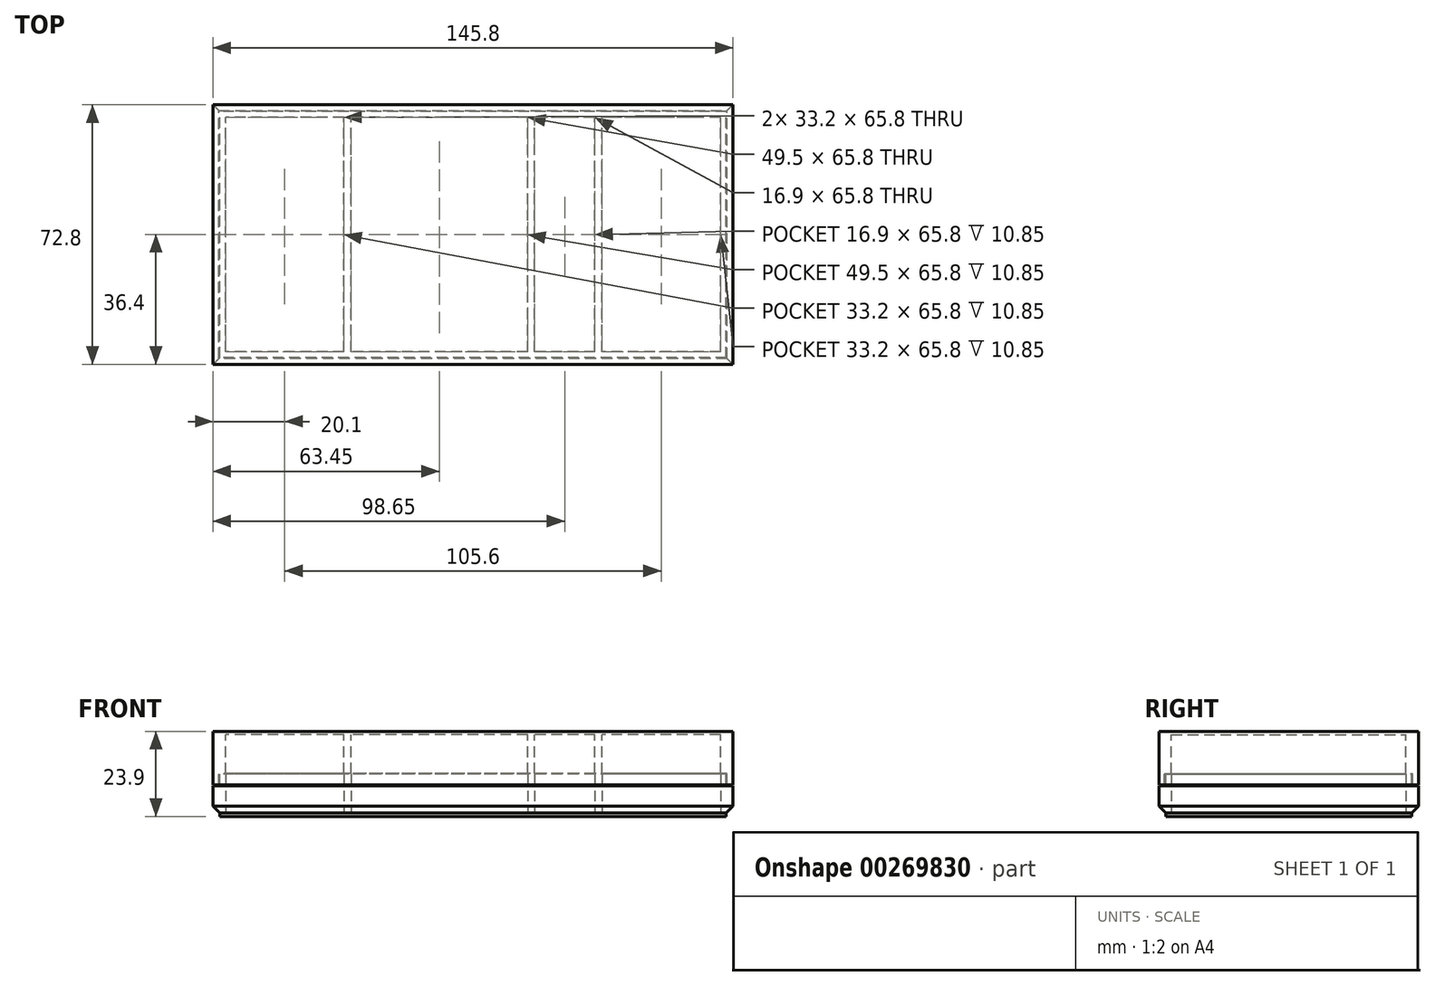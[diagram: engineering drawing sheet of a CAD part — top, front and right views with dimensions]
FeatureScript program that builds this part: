
annotation { "Feature Type Name" : "Feature", "Feature Type Description" : "" }
export const myFeature = defineFeature(function(context is Context, id is Id, definition is map)
    precondition{}
    {
        {
            assignVariable(context, id + "F0", {"name" : "chaff", "anyValue" : .3});
        }
        {
            assignVariable(context, id + "F1", {"name" : "basethick", "anyValue" : 1});
        }
        {
            assignVariable(context, id + "F2", {"name" : "unitTokenHeight", "anyValue" : 20.5});
        }
        {
            assignVariable(context, id + "F3", {"name" : "lidrimdepth", "anyValue" : 3});
        }
        {
            var Q0;
            Q0=qCreatedBy(makeId("Top.planeOp"),FACE);
            var sketch = newSketch(context, id + "F4", { "sketchPlane" : qUnion([Q0])});
            skLineSegment(sketch, "E0.bottom", {"start": v(72.9, -36.4) * mm, "end": v(-72.9, -36.4) * mm});
            skLineSegment(sketch, "E0.top", {"start": v(72.9, 36.4) * mm, "end": v(-72.9, 36.4) * mm});
            skLineSegment(sketch, "E0.left", {"start": v(72.9, -36.4) * mm, "end": v(72.9, 36.4) * mm});
            skLineSegment(sketch, "E0.right", {"start": v(-72.9, -36.4) * mm, "end": v(-72.9, 36.4) * mm});
            skPoint(sketch, "E0.middle", {"position": v(0, 0) * mm});
            skSolve(sketch);
        }
        {
            var Q0;
            Q0=qSketchRegion(id+"F4",true);
            extrude(context, id + "F5", {"entities" : qUnion([Q0]), "depth" : (getVariable(context, 'basethick')) * mm});
        }
        {
            var Q0;
            Q0=makeQuery(id+"F5.opExtrude","CAP_FACE",FACE,{"disambiguationData":[OSD([sQuery(id+"F4.wireOp",EDGE,"E0.bottom"),sQuery(id+"F4.wireOp",EDGE,"E0.top"),sQuery(id+"F4.wireOp",EDGE,"E0.left"),sQuery(id+"F4.wireOp",EDGE,"E0.right")])],"isStart":false});
            var sketch = newSketch(context, id + "F6", { "sketchPlane" : qUnion([Q0])});
            skLineSegment(sketch, "E1.bottom", {"start": v(69.4, -32.9) * mm, "end": v(-69.4, -32.9) * mm});
            skLineSegment(sketch, "E1.top", {"start": v(69.4, 32.9) * mm, "end": v(-69.4, 32.9) * mm});
            skLineSegment(sketch, "E1.left", {"start": v(69.4, -32.9) * mm, "end": v(69.4, 32.9) * mm});
            skLineSegment(sketch, "E1.right", {"start": v(-69.4, -32.9) * mm, "end": v(-69.4, 32.9) * mm});
            skPoint(sketch, "E1.middle", {"position": v(0, 0) * mm});
            skLineSegment(sketch, "E2", {"start": v(0, 32.9) * mm, "end": v(0, 36.4) * mm, "construction": true});
            skLineSegment(sketch, "E3.0", {"start": v(-72.9, -36.4) * mm, "end": v(-72.9, 36.4) * mm});
            skLineSegment(sketch, "E4.0", {"start": v(72.9, -36.4) * mm, "end": v(-72.9, -36.4) * mm});
            skLineSegment(sketch, "E5.0", {"start": v(72.9, -36.4) * mm, "end": v(72.9, 36.4) * mm});
            skLineSegment(sketch, "E6.0", {"start": v(72.9, 36.4) * mm, "end": v(-72.9, 36.4) * mm});
            skLineSegment(sketch, "E7", {"start": v(-72.9, 0) * mm, "end": v(-69.4, 0) * mm, "construction": true});
            skSolve(sketch);
        }
        {
            var Q0;
            Q0=qSketchRegion(id+"F6",true);
            extrude(context, id + "F7", {"entities" : qUnion([Q0]), "operationType" : NewBodyOperationType.ADD, "depth" : (getVariable(context, 'unitTokenHeight') / 2 + getVariable(context, 'chaff') * 2) * mm});
        }
        {
            var Q0;
            Q0=makeQuery(id+"F7.opExtrude","SWEPT_FACE",FACE,{"disambiguationData":[OSD([sQuery(id+"F6.wireOp",EDGE,"E1.top")])]});
            var sketch = newSketch(context, id + "F8", { "sketchPlane" : qUnion([Q0])});
            skLineSegment(sketch, "E8", {"start": v(-69.4, 11.85) * mm, "end": v(-36.2, 11.85) * mm, "construction": true});
            skLineSegment(sketch, "E9.bottom", {"start": v(-36.2, 11.85) * mm, "end": v(-34.2, 11.85) * mm});
            skLineSegment(sketch, "E9.top", {"start": v(-36.2, 1) * mm, "end": v(-34.2, 1) * mm});
            skLineSegment(sketch, "E9.left", {"start": v(-36.2, 11.85) * mm, "end": v(-36.2, 1) * mm});
            skLineSegment(sketch, "E9.right", {"start": v(-34.2, 11.85) * mm, "end": v(-34.2, 1) * mm});
            skLineSegment(sketch, "E10", {"start": v(-34.2, 11.85) * mm, "end": v(15.3, 11.85) * mm, "construction": true});
            skLineSegment(sketch, "E11.bottom", {"start": v(15.3, 11.85) * mm, "end": v(17.3, 11.85) * mm});
            skLineSegment(sketch, "E11.top", {"start": v(15.3, 1) * mm, "end": v(17.3, 1) * mm});
            skLineSegment(sketch, "E11.left", {"start": v(15.3, 11.85) * mm, "end": v(15.3, 1) * mm});
            skLineSegment(sketch, "E11.right", {"start": v(17.3, 11.85) * mm, "end": v(17.3, 1) * mm});
            skLineSegment(sketch, "E12", {"start": v(17.3, 11.85) * mm, "end": v(34.2, 11.85) * mm, "construction": true});
            skLineSegment(sketch, "E13.bottom", {"start": v(34.2, 11.85) * mm, "end": v(36.2, 11.85) * mm});
            skLineSegment(sketch, "E13.top", {"start": v(34.2, 1) * mm, "end": v(36.2, 1) * mm});
            skLineSegment(sketch, "E13.left", {"start": v(34.2, 11.85) * mm, "end": v(34.2, 1) * mm});
            skLineSegment(sketch, "E13.right", {"start": v(36.2, 11.85) * mm, "end": v(36.2, 1) * mm});
            skLineSegment(sketch, "E14", {"start": v(36.2, 11.85) * mm, "end": v(69.4, 11.85) * mm, "construction": true});
            skSolve(sketch);
        }
        {
            var Q0;
            Q0=makeQuery(id+"F8.imprint","IMPRINT",FACE,{"disambiguationData":[TD([[makeQuery(id+"F8.imprint","IMPRINT",EDGE,{"derivedFrom":sQuery(id+"F8.wireOp",EDGE,"E9.bottom")}),1.0]])]});
            var Q1;
            Q1=makeQuery(id+"F8.imprint","IMPRINT",FACE,{"disambiguationData":[TD([[makeQuery(id+"F8.imprint","IMPRINT",EDGE,{"derivedFrom":sQuery(id+"F8.wireOp",EDGE,"E11.bottom")}),1.0]])]});
            var Q2;
            Q2=makeQuery(id+"F8.imprint","IMPRINT",FACE,{"disambiguationData":[TD([[makeQuery(id+"F8.imprint","IMPRINT",EDGE,{"derivedFrom":sQuery(id+"F8.wireOp",EDGE,"E13.bottom")}),1.0]])]});
            var Q3;
            Q3=makeQuery(id+"F7.opExtrude","SWEPT_FACE",FACE,{"disambiguationData":[OSD([sQuery(id+"F6.wireOp",EDGE,"E1.bottom")])]});
            extrude(context, id + "F9", {"entities" : qUnion([Q0, Q1, Q2]), "operationType" : NewBodyOperationType.ADD, "endBound" : BoundingType.UP_TO_SURFACE, "endBoundEntityFace" : qUnion([Q3]), "depth" : 25 * mm});
        }
        {
            var Q0;
            {var subQ0=sQuery(id+"F8.wireOp",EDGE,"b7063ba6-163c-4e90-9692-3a0a1676d49b.0");var subQ1=sQuery(id+"F8.wireOp",EDGE,"5b0bd29a-2a72-4641-92b4-ce3cebaaf724.1.0.1");var subQ2=sQuery(id+"F8.wireOp",EDGE,"5b0bd29a-2a72-4641-92b4-ce3cebaaf724.2.0.1");Q0=makeQuery(id+"F9.boolean.opBoolean","MERGE",FACE,{"derivedFrom":[makeQuery(id+"F7.opExtrude","CAP_FACE",FACE,{"disambiguationData":[OSD([sQuery(id+"F6.wireOp",EDGE,"E1.bottom"),sQuery(id+"F6.wireOp",EDGE,"E1.top"),sQuery(id+"F6.wireOp",EDGE,"E1.left"),sQuery(id+"F6.wireOp",EDGE,"E1.right"),sQuery(id+"F6.wireOp",EDGE,"E3.0"),sQuery(id+"F6.wireOp",EDGE,"E4.0"),sQuery(id+"F6.wireOp",EDGE,"E5.0"),sQuery(id+"F6.wireOp",EDGE,"E6.0")])],"isStart":false}),makeQuery(id+"F9.opExtrude","SWEPT_FACE",FACE,{"disambiguationData":[OSD([subQ0]),TDD([makeQuery(id+"F8.imprint","IMPRINT",EDGE,{"disambiguationData":[TD([[makeQuery(id+"F8.imprint","INTERSECT",VERTEX,{"derivedFrom":[sQuery(id+"F8.wireOp",EDGE,"ed8556cc-012e-414f-a647-4d99696943b9.0"),subQ0]}),-1.0]])],"derivedFrom":subQ0})])]}),makeQuery(id+"F9.opExtrude","SWEPT_FACE",FACE,{"disambiguationData":[OSD([subQ0]),TDD([makeQuery(id+"F8.imprint","IMPRINT",EDGE,{"disambiguationData":[TD([[makeQuery(id+"F8.imprint","INTERSECT",VERTEX,{"disambiguationData":[OD(1.0)],"derivedFrom":[subQ2,subQ0]}),1.0]])],"derivedFrom":subQ0})])]}),makeQuery(id+"F9.opExtrude","SWEPT_FACE",FACE,{"disambiguationData":[OSD([subQ0]),TDD([makeQuery(id+"F8.imprint","IMPRINT",EDGE,{"disambiguationData":[TD([[makeQuery(id+"F8.imprint","INTERSECT",VERTEX,{"disambiguationData":[OD(1.0)],"derivedFrom":[subQ1,subQ0]}),1.0]])],"derivedFrom":subQ0})])]}),makeQuery(id+"F9.opExtrude","SWEPT_FACE",FACE,{"disambiguationData":[OSD([subQ0]),TDD([makeQuery(id+"F8.imprint","IMPRINT",EDGE,{"disambiguationData":[TD([[makeQuery(id+"F8.imprint","INTERSECT",VERTEX,{"derivedFrom":[sQuery(id+"F8.wireOp",EDGE,"CCxmkI6E-hdHg-CZTa-q9Gf-agiM700yoBqG"),subQ0]}),1.0]])],"derivedFrom":subQ0})])]})]});}
            cPlane(context, id + "F10", {"entities" : qUnion([Q0]), "cplaneType" : CPlaneType.OFFSET, "offset" : .1 * mm, "width" : 150 * mm, "height" : 150 * mm});
        }
        {
            var Q0;
            Q0=makeQuery(id+"F5.opExtrude","SWEPT_BODY",BODY,{"disambiguationData":[OSD([sQuery(id+"F4.wireOp",EDGE,"E0.bottom"),sQuery(id+"F4.wireOp",EDGE,"E0.top"),sQuery(id+"F4.wireOp",EDGE,"E0.left"),sQuery(id+"F4.wireOp",EDGE,"E0.right")])]});
            var Q1;
            Q1=qCreatedBy(id+"F10.planeOp",FACE);
            mirror(context, id + "F11", {"entities" : qUnion([Q0]), "mirrorPlane" : qUnion([Q1])});
        }
        {
            var Q0;
            {var subQ0=sQuery(id+"F8.wireOp",EDGE,"b7063ba6-163c-4e90-9692-3a0a1676d49b.0");var subQ1=sQuery(id+"F8.wireOp",EDGE,"5b0bd29a-2a72-4641-92b4-ce3cebaaf724.1.0.1");var subQ2=sQuery(id+"F8.wireOp",EDGE,"5b0bd29a-2a72-4641-92b4-ce3cebaaf724.2.0.1");Q0=makeQuery(id+"F9.boolean.opBoolean","MERGE",FACE,{"derivedFrom":[makeQuery(id+"F7.opExtrude","CAP_FACE",FACE,{"disambiguationData":[OSD([sQuery(id+"F6.wireOp",EDGE,"E1.bottom"),sQuery(id+"F6.wireOp",EDGE,"E1.top"),sQuery(id+"F6.wireOp",EDGE,"E1.left"),sQuery(id+"F6.wireOp",EDGE,"E1.right"),sQuery(id+"F6.wireOp",EDGE,"E3.0"),sQuery(id+"F6.wireOp",EDGE,"E4.0"),sQuery(id+"F6.wireOp",EDGE,"E5.0"),sQuery(id+"F6.wireOp",EDGE,"E6.0")])],"isStart":false}),makeQuery(id+"F9.opExtrude","SWEPT_FACE",FACE,{"disambiguationData":[OSD([subQ0]),TDD([makeQuery(id+"F8.imprint","IMPRINT",EDGE,{"disambiguationData":[TD([[makeQuery(id+"F8.imprint","INTERSECT",VERTEX,{"derivedFrom":[sQuery(id+"F8.wireOp",EDGE,"ed8556cc-012e-414f-a647-4d99696943b9.0"),subQ0]}),-1.0]])],"derivedFrom":subQ0})])]}),makeQuery(id+"F9.opExtrude","SWEPT_FACE",FACE,{"disambiguationData":[OSD([subQ0]),TDD([makeQuery(id+"F8.imprint","IMPRINT",EDGE,{"disambiguationData":[TD([[makeQuery(id+"F8.imprint","INTERSECT",VERTEX,{"disambiguationData":[OD(1.0)],"derivedFrom":[subQ2,subQ0]}),1.0]])],"derivedFrom":subQ0})])]}),makeQuery(id+"F9.opExtrude","SWEPT_FACE",FACE,{"disambiguationData":[OSD([subQ0]),TDD([makeQuery(id+"F8.imprint","IMPRINT",EDGE,{"disambiguationData":[TD([[makeQuery(id+"F8.imprint","INTERSECT",VERTEX,{"disambiguationData":[OD(1.0)],"derivedFrom":[subQ1,subQ0]}),1.0]])],"derivedFrom":subQ0})])]}),makeQuery(id+"F9.opExtrude","SWEPT_FACE",FACE,{"disambiguationData":[OSD([subQ0]),TDD([makeQuery(id+"F8.imprint","IMPRINT",EDGE,{"disambiguationData":[TD([[makeQuery(id+"F8.imprint","INTERSECT",VERTEX,{"derivedFrom":[sQuery(id+"F8.wireOp",EDGE,"CCxmkI6E-hdHg-CZTa-q9Gf-agiM700yoBqG"),subQ0]}),1.0]])],"derivedFrom":subQ0})])]})]});}
            var sketch = newSketch(context, id + "F12", { "sketchPlane" : qUnion([Q0])});
            skLineSegment(sketch, "E15.0", {"start": v(72.9, 36.4) * mm, "end": v(-72.9, 36.4) * mm});
            skLineSegment(sketch, "E16.0", {"start": v(-72.9, -36.4) * mm, "end": v(-72.9, 36.4) * mm});
            skLineSegment(sketch, "E17.0", {"start": v(72.9, -36.4) * mm, "end": v(-72.9, -36.4) * mm});
            skLineSegment(sketch, "E18.0", {"start": v(72.9, -36.4) * mm, "end": v(72.9, 36.4) * mm});
            skLineSegment(sketch, "E19.0", {"start": v(71, 34.5) * mm, "end": v(-71, 34.5) * mm});
            skLineSegment(sketch, "E19.1", {"start": v(71, -34.5) * mm, "end": v(71, 34.5) * mm});
            skLineSegment(sketch, "E19.2", {"start": v(71, -34.5) * mm, "end": v(-71, -34.5) * mm});
            skLineSegment(sketch, "E19.3", {"start": v(-71, -34.5) * mm, "end": v(-71, 34.5) * mm});
            skSolve(sketch);
        }
        {
            var Q0;
            Q0=makeQuery(id+"F12.imprint","IMPRINT",FACE,{"disambiguationData":[TD([[makeQuery(id+"F12.imprint","IMPRINT",EDGE,{"derivedFrom":sQuery(id+"F12.wireOp",EDGE,"E15.0")}),1.0]])]});
            extrude(context, id + "F13", {"entities" : qUnion([Q0]), "operationType" : NewBodyOperationType.REMOVE, "oppositeDirection" : true, "depth" : (getVariable(context, 'lidrimdepth') + getVariable(context, 'chaff')) * mm});
        }
        {
            var Q0;
            Q0=makeQuery(id+"F5.opExtrude","CAP_FACE",FACE,{"disambiguationData":[OSD([sQuery(id+"F4.wireOp",EDGE,"E0.bottom"),sQuery(id+"F4.wireOp",EDGE,"E0.top"),sQuery(id+"F4.wireOp",EDGE,"E0.left"),sQuery(id+"F4.wireOp",EDGE,"E0.right")])],"isStart":true});
            var sketch = newSketch(context, id + "F14", { "sketchPlane" : qUnion([Q0])});
            skLineSegment(sketch, "E20.0", {"start": v(72.9, 36.4) * mm, "end": v(-72.9, 36.4) * mm});
            skLineSegment(sketch, "E21.0", {"start": v(-72.9, 36.4) * mm, "end": v(-72.9, -36.4) * mm});
            skLineSegment(sketch, "E22.0", {"start": v(72.9, 36.4) * mm, "end": v(72.9, -36.4) * mm});
            skLineSegment(sketch, "E23.0", {"start": v(72.9, -36.4) * mm, "end": v(-72.9, -36.4) * mm});
            skLineSegment(sketch, "E24.0", {"start": v(71, 34.5) * mm, "end": v(-71, 34.5) * mm});
            skLineSegment(sketch, "E24.1", {"start": v(71, 34.5) * mm, "end": v(71, -34.5) * mm});
            skLineSegment(sketch, "E24.2", {"start": v(71, -34.5) * mm, "end": v(-71, -34.5) * mm});
            skLineSegment(sketch, "E24.3", {"start": v(-71, 34.5) * mm, "end": v(-71, -34.5) * mm});
            skSolve(sketch);
        }
        {
            var Q0;
            Q0=qSketchRegion(id+"F14",true);
            extrude(context, id + "F15", {"entities" : qUnion([Q0]), "operationType" : NewBodyOperationType.REMOVE, "oppositeDirection" : true, "depth" : (getVariable(context, 'lidrimdepth')) * mm});
        }
        {
            var Q0;
            Q0=makeQuery(id+"F15.boolean.opBoolean","COPY",EDGE,{"derivedFrom":makeQuery(id+"F15.opExtrude","CAP_EDGE",EDGE,{"disambiguationData":[OSD([sQuery(id+"F14.wireOp",EDGE,"E24.0")])],"isStart":false})});
            var Q1;
            Q1=makeQuery(id+"F15.boolean.opBoolean","COPY",EDGE,{"derivedFrom":makeQuery(id+"F15.opExtrude","CAP_EDGE",EDGE,{"disambiguationData":[OSD([sQuery(id+"F14.wireOp",EDGE,"E24.3")])],"isStart":false})});
            var Q2;
            Q2=makeQuery(id+"F15.boolean.opBoolean","COPY",EDGE,{"derivedFrom":makeQuery(id+"F15.opExtrude","CAP_EDGE",EDGE,{"disambiguationData":[OSD([sQuery(id+"F14.wireOp",EDGE,"E24.2")])],"isStart":false})});
            var Q3;
            Q3=makeQuery(id+"F15.boolean.opBoolean","COPY",EDGE,{"derivedFrom":makeQuery(id+"F15.opExtrude","CAP_EDGE",EDGE,{"disambiguationData":[OSD([sQuery(id+"F14.wireOp",EDGE,"E24.1")])],"isStart":false})});
            chamfer(context, id + "F16", {"entities" : qUnion([Q0, Q1, Q2, Q3]), "width" : 2 * mm, "tangentPropagation" : true});
        }
        {
            var Q0;
            {var subQ0=sQuery(id+"F8.wireOp",EDGE,"b7063ba6-163c-4e90-9692-3a0a1676d49b.0");var subQ1=sQuery(id+"F8.wireOp",EDGE,"5b0bd29a-2a72-4641-92b4-ce3cebaaf724.1.0.1");var subQ2=sQuery(id+"F8.wireOp",EDGE,"5b0bd29a-2a72-4641-92b4-ce3cebaaf724.2.0.1");Q0=makeQuery(id+"F11.opPattern","COPY",FACE,{"derivedFrom":makeQuery(id+"F9.boolean.opBoolean","MERGE",FACE,{"derivedFrom":[makeQuery(id+"F7.opExtrude","CAP_FACE",FACE,{"disambiguationData":[OSD([sQuery(id+"F6.wireOp",EDGE,"E1.bottom"),sQuery(id+"F6.wireOp",EDGE,"E1.top"),sQuery(id+"F6.wireOp",EDGE,"E1.left"),sQuery(id+"F6.wireOp",EDGE,"E1.right"),sQuery(id+"F6.wireOp",EDGE,"E3.0"),sQuery(id+"F6.wireOp",EDGE,"E4.0"),sQuery(id+"F6.wireOp",EDGE,"E5.0"),sQuery(id+"F6.wireOp",EDGE,"E6.0")])],"isStart":false}),makeQuery(id+"F9.opExtrude","SWEPT_FACE",FACE,{"disambiguationData":[OSD([subQ0]),TDD([makeQuery(id+"F8.imprint","IMPRINT",EDGE,{"disambiguationData":[TD([[makeQuery(id+"F8.imprint","INTERSECT",VERTEX,{"derivedFrom":[sQuery(id+"F8.wireOp",EDGE,"ed8556cc-012e-414f-a647-4d99696943b9.0"),subQ0]}),-1.0]])],"derivedFrom":subQ0})])]}),makeQuery(id+"F9.opExtrude","SWEPT_FACE",FACE,{"disambiguationData":[OSD([subQ0]),TDD([makeQuery(id+"F8.imprint","IMPRINT",EDGE,{"disambiguationData":[TD([[makeQuery(id+"F8.imprint","INTERSECT",VERTEX,{"disambiguationData":[OD(1.0)],"derivedFrom":[subQ2,subQ0]}),1.0]])],"derivedFrom":subQ0})])]}),makeQuery(id+"F9.opExtrude","SWEPT_FACE",FACE,{"disambiguationData":[OSD([subQ0]),TDD([makeQuery(id+"F8.imprint","IMPRINT",EDGE,{"disambiguationData":[TD([[makeQuery(id+"F8.imprint","INTERSECT",VERTEX,{"disambiguationData":[OD(1.0)],"derivedFrom":[subQ1,subQ0]}),1.0]])],"derivedFrom":subQ0})])]}),makeQuery(id+"F9.opExtrude","SWEPT_FACE",FACE,{"disambiguationData":[OSD([subQ0]),TDD([makeQuery(id+"F8.imprint","IMPRINT",EDGE,{"disambiguationData":[TD([[makeQuery(id+"F8.imprint","INTERSECT",VERTEX,{"derivedFrom":[sQuery(id+"F8.wireOp",EDGE,"CCxmkI6E-hdHg-CZTa-q9Gf-agiM700yoBqG"),subQ0]}),1.0]])],"derivedFrom":subQ0})])]})]}),"instanceName":"1"});}
            var sketch = newSketch(context, id + "F17", { "sketchPlane" : qUnion([Q0])});
            skPoint(sketch, "E25.0", {"position": v(-69.4, 32.9) * mm});
            skPoint(sketch, "E26.0", {"position": v(69.4, -32.9) * mm});
            skPoint(sketch, "E27.0", {"position": v(-69.4, -32.9) * mm});
            skLineSegment(sketch, "E28", {"start": v(69.4, 32.9) * mm, "end": v(-69.4, 32.9) * mm, "construction": true});
            skLineSegment(sketch, "E29", {"start": v(-69.4, -32.9) * mm, "end": v(69.4, -32.9) * mm, "construction": true});
            skLineSegment(sketch, "E30", {"start": v(69.4, 32.9) * mm, "end": v(69.4, -32.9) * mm, "construction": true});
            skLineSegment(sketch, "E31", {"start": v(-69.4, 32.9) * mm, "end": v(-69.4, -32.9) * mm, "construction": true});
            skLineSegment(sketch, "E32.0", {"start": v(71.3, 34.8) * mm, "end": v(-71.3, 34.8) * mm});
            skLineSegment(sketch, "E32.1", {"start": v(71.3, 34.8) * mm, "end": v(71.3, -34.8) * mm});
            skLineSegment(sketch, "E32.2", {"start": v(-71.3, -34.8) * mm, "end": v(71.3, -34.8) * mm});
            skLineSegment(sketch, "E32.3", {"start": v(-71.3, 34.8) * mm, "end": v(-71.3, -34.8) * mm});
            skLineSegment(sketch, "E33.0", {"start": v(72.9, 36.4) * mm, "end": v(-72.9, 36.4) * mm});
            skLineSegment(sketch, "E34.0", {"start": v(72.9, 36.4) * mm, "end": v(72.9, -36.4) * mm});
            skLineSegment(sketch, "E35.0", {"start": v(72.9, -36.4) * mm, "end": v(-72.9, -36.4) * mm});
            skLineSegment(sketch, "E36.0", {"start": v(-72.9, 36.4) * mm, "end": v(-72.9, -36.4) * mm});
            skPoint(sketch, "E37", {"position": v(69.4, 32.9) * mm});
            skSolve(sketch);
        }
        {
            var Q0;
            Q0=qSketchRegion(id+"F17",true);
            extrude(context, id + "F18", {"entities" : qUnion([Q0]), "operationType" : NewBodyOperationType.ADD, "depth" : 3.2 * mm});
        }
    });
